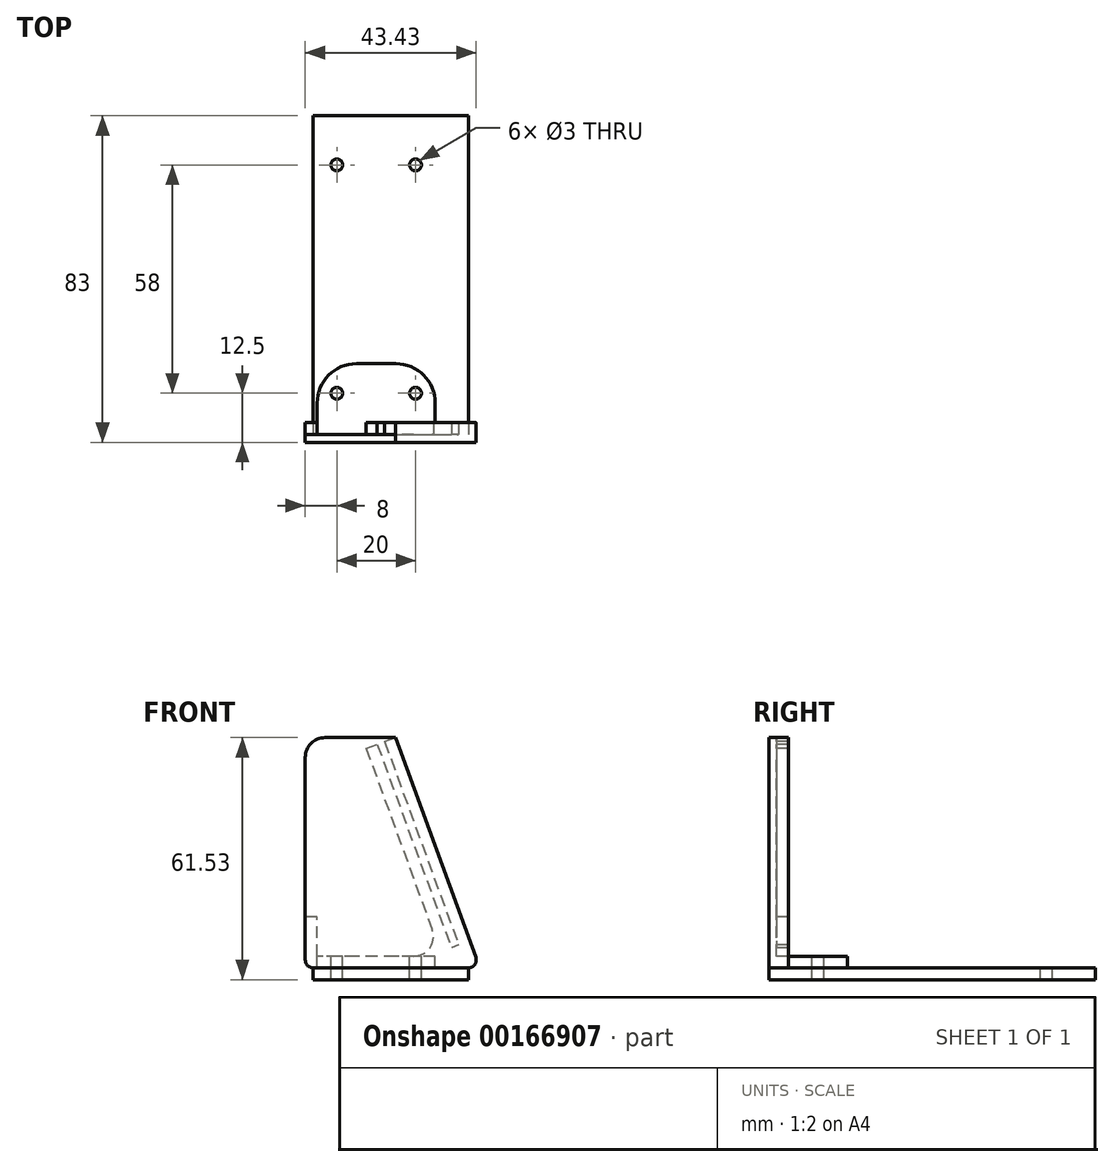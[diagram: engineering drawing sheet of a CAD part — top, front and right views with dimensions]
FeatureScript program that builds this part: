
annotation { "Feature Type Name" : "Feature", "Feature Type Description" : "" }
export const myFeature = defineFeature(function(context is Context, id is Id, definition is map)
    precondition{}
    {
        {
            var Q0;
            Q0=qCreatedBy(makeId("Front.planeOp"),FACE);
            var sketch = newSketch(context, id + "F0", { "sketchPlane" : qUnion([Q0])});
            skLineSegment(sketch, "E0", {"start": v(0, 0) * mm, "end": v(37, 0) * mm, "construction": true});
            skLineSegment(sketch, "E1", {"start": v(37, 0) * mm, "end": v(17.16, 54.5) * mm, "construction": true});
            skLineSegment(sketch, "E2", {"start": v(0, 0) * mm, "end": v(0, 10) * mm});
            skLineSegment(sketch, "E3", {"start": v(0, 10) * mm, "end": v(-3, 10) * mm});
            skLineSegment(sketch, "E4", {"start": v(-3, 10) * mm, "end": v(-3, -1) * mm});
            skLineSegment(sketch, "E5", {"start": v(-1, -3) * mm, "end": v(38.43, -3) * mm});
            skLineSegment(sketch, "E6", {"start": v(40.3, -0.32) * mm, "end": v(19.98, 55.53) * mm});
            skLineSegment(sketch, "E7", {"start": v(0, 10) * mm, "end": v(0, 0) * mm});
            skLineSegment(sketch, "E8", {"start": v(15.28, 53.82) * mm, "end": v(34.1, 2.14) * mm});
            skLineSegment(sketch, "E9", {"start": v(17.16, 54.5) * mm, "end": v(35.97, 2.82) * mm});
            skLineSegment(sketch, "E10", {"start": v(35.97, 2.82) * mm, "end": v(34.1, 2.14) * mm});
            skLineSegment(sketch, "E11", {"start": v(12.46, 52.8) * mm, "end": v(29.24, 6.71) * mm});
            skLineSegment(sketch, "E12", {"start": v(24.54, 0) * mm, "end": v(0, 0) * mm});
            skLineSegment(sketch, "E13", {"start": v(12.46, 52.8) * mm, "end": v(15.28, 53.82) * mm});
            skLineSegment(sketch, "E14", {"start": v(17.16, 54.5) * mm, "end": v(19.98, 55.53) * mm});
            skPoint(sketch, "E15.visualSharp", {"position": v(31.68, 0) * mm});
            skArc(sketch, "E15.filletArc", {"start": v(24.54, 0) * mm, "mid": v(28.63, 2.13) * mm, "end": v(29.24, 6.71) * mm});
            skPoint(sketch, "E16.visualSharp", {"position": v(41.28, -3) * mm});
            skArc(sketch, "E16.filletArc", {"start": v(38.43, -3) * mm, "mid": v(40.07, -2.15) * mm, "end": v(40.3, -0.32) * mm});
            skLineSegment(sketch, "E17.bottom", {"start": v(0, 0) * mm, "end": v(26, 0) * mm, "construction": true});
            skLineSegment(sketch, "E17.top", {"start": v(0, 21) * mm, "end": v(26, 21) * mm, "construction": true});
            skLineSegment(sketch, "E17.left", {"start": v(0, 0) * mm, "end": v(0, 21) * mm, "construction": true});
            skLineSegment(sketch, "E17.right", {"start": v(26, 0) * mm, "end": v(26, 21) * mm, "construction": true});
            skLineSegment(sketch, "E18", {"start": v(22, 21) * mm, "end": v(22, 0) * mm, "construction": true});
            skPoint(sketch, "E19.visualSharp", {"position": v(-3, -3) * mm});
            skArc(sketch, "E19.filletArc", {"start": v(-3, -1) * mm, "mid": v(-2.41, -2.41) * mm, "end": v(-1, -3) * mm});
            skSolve(sketch);
        }
        {
            var Q0;
            Q0 = qSketchRegion(id + "F0", true);
            extrude(context, id + "F1", {"entities" : qUnion([Q0]), "oppositeDirection" : true, "depth" : 3 * mm});
        }
        {
            var Q0;
            Q0=qCreatedBy(makeId("Front.planeOp"),FACE);
            var sketch = newSketch(context, id + "F2", { "sketchPlane" : qUnion([Q0])});
            skLineSegment(sketch, "E20.0.2", {"start": v(-3, 10) * mm, "end": v(-3, 10) * mm});
            skArc(sketch, "E20.0.4", {"start": v(38.43, -3) * mm, "mid": v(40.07, -2.15) * mm, "end": v(40.3, -0.32) * mm});
            skLineSegment(sketch, "E20.0.5", {"start": v(40.3, -0.32) * mm, "end": v(19.98, 55.53) * mm});
            skLineSegment(sketch, "E21", {"start": v(-3, 10) * mm, "end": v(-3, 50.53) * mm});
            skLineSegment(sketch, "E22", {"start": v(2, 55.53) * mm, "end": v(19.98, 55.53) * mm});
            skPoint(sketch, "E23.visualSharp", {"position": v(-3, 55.53) * mm});
            skArc(sketch, "E23.filletArc", {"start": v(2, 55.53) * mm, "mid": v(-1.54, 54.06) * mm, "end": v(-3, 50.53) * mm});
            skLineSegment(sketch, "E24.0", {"start": v(-3, 10) * mm, "end": v(-3, -1) * mm});
            skArc(sketch, "E24.1", {"start": v(-3, -1) * mm, "mid": v(-2.41, -2.41) * mm, "end": v(-1, -3) * mm});
            skLineSegment(sketch, "E24.2", {"start": v(-1, -3) * mm, "end": v(38.43, -3) * mm});
            skSolve(sketch);
        }
        {
            var Q0;
            Q0 = qSketchRegion(id + "F2", true);
            extrude(context, id + "F3", {"entities" : qUnion([Q0]), "operationType" : NewBodyOperationType.ADD, "depth" : 2 * mm});
        }
        {
            var Q0;
            Q0=makeQuery(id+"F1.opExtrude","CAP_FACE",FACE,{"disambiguationData":[OSD([sQuery(id+"F0.wireOp",EDGE,"E3"),sQuery(id+"F0.wireOp",EDGE,"E4"),sQuery(id+"F0.wireOp",EDGE,"E5"),sQuery(id+"F0.wireOp",EDGE,"E6"),sQuery(id+"F0.wireOp",EDGE,"E7"),sQuery(id+"F0.wireOp",EDGE,"E8"),sQuery(id+"F0.wireOp",EDGE,"E9"),sQuery(id+"F0.wireOp",EDGE,"E10"),sQuery(id+"F0.wireOp",EDGE,"E11"),sQuery(id+"F0.wireOp",EDGE,"E12"),sQuery(id+"F0.wireOp",EDGE,"E13"),sQuery(id+"F0.wireOp",EDGE,"E14"),sQuery(id+"F0.wireOp",EDGE,"E15.filletArc"),sQuery(id+"F0.wireOp",EDGE,"E16.filletArc"),sQuery(id+"F0.wireOp",EDGE,"E19.filletArc")])],"isStart":false});
            var sketch = newSketch(context, id + "F4", { "sketchPlane" : qUnion([Q0])});
            skLineSegment(sketch, "E25.bottom", {"start": v(-30, -3) * mm, "end": v(0, -3) * mm});
            skLineSegment(sketch, "E25.top", {"start": v(-30, 0) * mm, "end": v(0, 0) * mm});
            skLineSegment(sketch, "E25.left", {"start": v(-30, -3) * mm, "end": v(-30, 0) * mm});
            skLineSegment(sketch, "E25.right", {"start": v(0, -3) * mm, "end": v(0, 0) * mm});
            skSolve(sketch);
        }
        {
            var Q0;
            Q0 = qSketchRegion(id + "F4", true);
            extrude(context, id + "F5", {"entities" : qUnion([Q0]), "operationType" : NewBodyOperationType.ADD, "depth" : 15 * mm});
        }
        {
            var Q0;
            Q0=makeQuery(id+"F5.boolean.opBoolean","MERGE",FACE,{"derivedFrom":[makeQuery(id+"F1.opExtrude","SWEPT_FACE",FACE,{"disambiguationData":[OSD([sQuery(id+"F0.wireOp",EDGE,"E12")])]}),makeQuery(id+"F5.opExtrude","SWEPT_FACE",FACE,{"disambiguationData":[OSD([sQuery(id+"F4.wireOp",EDGE,"E25.top")])]})]});
            var sketch = newSketch(context, id + "F6", { "sketchPlane" : qUnion([Q0])});
            skLineSegment(sketch, "E26", {"start": v(0, 0) * mm, "end": v(0, 18) * mm, "construction": true});
            skLineSegment(sketch, "E27", {"start": v(0, 18) * mm, "end": v(0, 10.5) * mm, "construction": true});
            skLineSegment(sketch, "E28", {"start": v(0, 10.5) * mm, "end": v(30, 10.5) * mm, "construction": true});
            skCircle(sketch, "E29", {"center": v(25, 10.5) * mm, "radius": 1.5 * mm});
            skCircle(sketch, "E30", {"center": v(5, 10.5) * mm, "radius": 1.5 * mm});
            skSolve(sketch);
        }
        {
            var Q0;
            Q0 = qSketchRegion(id + "F6", true);
            extrude(context, id + "F7", {"entities" : qUnion([Q0]), "operationType" : NewBodyOperationType.REMOVE, "endBound" : BoundingType.THROUGH_ALL, "oppositeDirection" : true, "depth" : 25 * mm});
        }
        {
            var Q0;
            Q0=makeQuery(id+"F5.opExtrude","CAP_EDGE",EDGE,{"disambiguationData":[OSD([sQuery(id+"F4.wireOp",EDGE,"E25.left")])],"isStart":false});
            var Q1;
            Q1=makeQuery(id+"F5.opExtrude","CAP_EDGE",EDGE,{"disambiguationData":[OSD([sQuery(id+"F4.wireOp",EDGE,"E25.right")])],"isStart":false});
            fillet(context, id + "F8", {"entities" : qUnion([Q0, Q1]), "radius" : 10 * mm, "tangentPropagation" : true, "allowEdgeOverflow" : false});
        }
        {
            var Q0;
            Q0=makeQuery(id+"F5.boolean.opBoolean","MERGE",FACE,{"derivedFrom":[makeQuery(id+"F3.boolean.opBoolean","MERGE",FACE,{"derivedFrom":[makeQuery(id+"F1.opExtrude","SWEPT_FACE",FACE,{"disambiguationData":[OSD([sQuery(id+"F0.wireOp",EDGE,"E5")])]}),makeQuery(id+"F3.opExtrude","SWEPT_FACE",FACE,{"disambiguationData":[OSD([sQuery(id+"F2.wireOp",EDGE,"E24.2")])]})]}),makeQuery(id+"F5.opExtrude","SWEPT_FACE",FACE,{"disambiguationData":[OSD([sQuery(id+"F4.wireOp",EDGE,"E25.bottom")])]})]});
            var sketch = newSketch(context, id + "F9", { "sketchPlane" : qUnion([Q0])});
            skLineSegment(sketch, "E31.bottom", {"start": v(38.43, 2) * mm, "end": v(-1, 2) * mm});
            skLineSegment(sketch, "E31.top", {"start": v(38.43, -81) * mm, "end": v(-1, -81) * mm});
            skLineSegment(sketch, "E31.left", {"start": v(38.43, 2) * mm, "end": v(38.43, -81) * mm});
            skLineSegment(sketch, "E31.right", {"start": v(-1, 2) * mm, "end": v(-1, -81) * mm});
            skCircle(sketch, "E32.0", {"center": v(25, -10.5) * mm, "radius": 1.5 * mm});
            skCircle(sketch, "E32.1", {"center": v(5, -10.5) * mm, "radius": 1.5 * mm});
            skLineSegment(sketch, "E33", {"start": v(38.43, -39.5) * mm, "end": v(-1, -39.5) * mm, "construction": true});
            skCircle(sketch, "E34.MirrorC", {"center": v(25, -68.5) * mm, "radius": 1.5 * mm});
            skCircle(sketch, "E35.MirrorC", {"center": v(5, -68.5) * mm, "radius": 1.5 * mm});
            skSolve(sketch);
        }
        {
            var Q0;
            Q0 = qSketchRegion(id + "F9", true);
            extrude(context, id + "F10", {"entities" : qUnion([Q0]), "depth" : 3 * mm});
        }
    });
